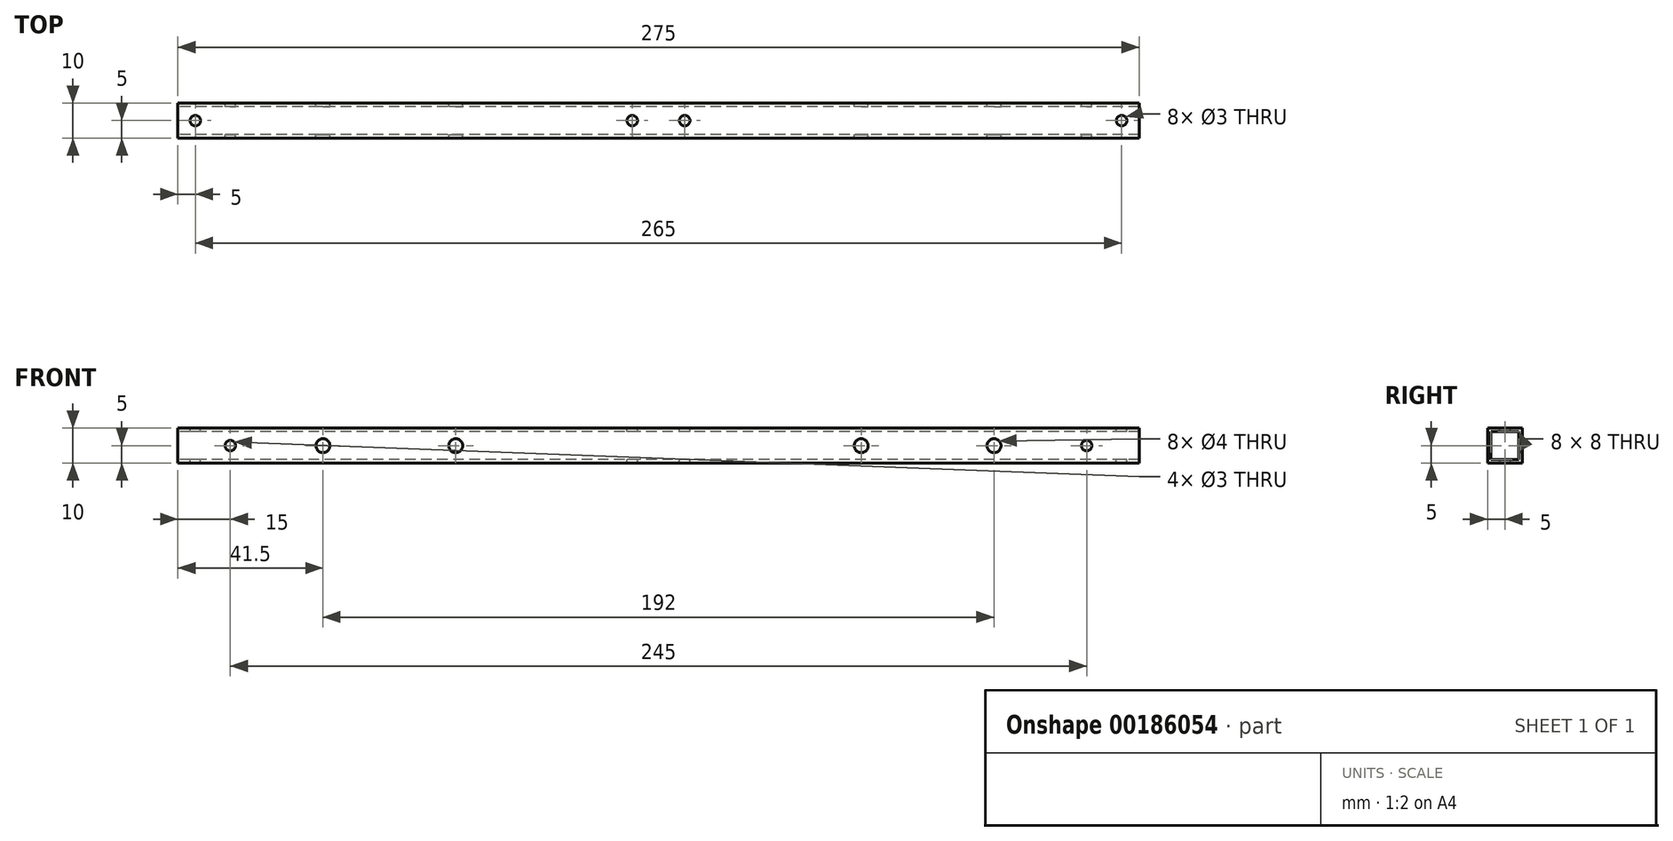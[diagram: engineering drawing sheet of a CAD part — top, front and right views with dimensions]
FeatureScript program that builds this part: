
annotation { "Feature Type Name" : "Feature", "Feature Type Description" : "" }
export const myFeature = defineFeature(function(context is Context, id is Id, definition is map)
    precondition{}
    {
        {
            var Q0;
            Q0=qCreatedBy(makeId("Right.planeOp"),FACE);
            var sketch = newSketch(context, id + "F0", { "sketchPlane" : qUnion([Q0])});
            skLineSegment(sketch, "E0.bottom", {"start": v(-5, -5) * mm, "end": v(5, -5) * mm});
            skLineSegment(sketch, "E0.top", {"start": v(-5, 5) * mm, "end": v(5, 5) * mm});
            skLineSegment(sketch, "E0.left", {"start": v(-5, -5) * mm, "end": v(-5, 5) * mm});
            skLineSegment(sketch, "E0.right", {"start": v(5, -5) * mm, "end": v(5, 5) * mm});
            skPoint(sketch, "E0.middle", {"position": v(0, 0) * mm});
            skLineSegment(sketch, "E1.bottom", {"start": v(-4, -4) * mm, "end": v(4, -4) * mm});
            skLineSegment(sketch, "E1.top", {"start": v(-4, 4) * mm, "end": v(4, 4) * mm});
            skLineSegment(sketch, "E1.left", {"start": v(-4, -4) * mm, "end": v(-4, 4) * mm});
            skLineSegment(sketch, "E1.right", {"start": v(4, -4) * mm, "end": v(4, 4) * mm});
            skSolve(sketch);
        }
        {
            var Q0;
            Q0 = qSketchRegion(id + "F0", true);
            extrude(context, id + "F1", {"entities" : qUnion([Q0]), "depth" : 275 * mm});
        }
        {
            var Q0;
            Q0=makeQuery(id+"F1.opExtrude","SWEPT_FACE",FACE,{"disambiguationData":[OSD([sQuery(id+"F0.wireOp",EDGE,"E0.top")])]});
            var sketch = newSketch(context, id + "F2", { "sketchPlane" : qUnion([Q0])});
            skLineSegment(sketch, "E2", {"start": v(0, 0) * mm, "end": v(275, 0) * mm, "construction": true});
            skLineSegment(sketch, "E3", {"start": v(137.5, -5) * mm, "end": v(137.5, 5) * mm, "construction": true});
            skCircle(sketch, "E4", {"center": v(130, 0) * mm, "radius": 1.5 * mm});
            skCircle(sketch, "E5", {"center": v(5, 0) * mm, "radius": 1.5 * mm});
            skCircle(sketch, "E6.MirrorC", {"center": v(145, 0) * mm, "radius": 1.5 * mm});
            skCircle(sketch, "E7.MirrorC", {"center": v(270, 0) * mm, "radius": 1.5 * mm});
            skSolve(sketch);
        }
        {
            var Q0;
            Q0 = qSketchRegion(id + "F2", true);
            extrude(context, id + "F3", {"entities" : qUnion([Q0]), "operationType" : NewBodyOperationType.REMOVE, "oppositeDirection" : true, "depth" : 25 * mm});
        }
        {
            var Q0;
            Q0=makeQuery(id+"F1.opExtrude","SWEPT_FACE",FACE,{"disambiguationData":[OSD([sQuery(id+"F0.wireOp",EDGE,"E0.right")])]});
            var sketch = newSketch(context, id + "F4", { "sketchPlane" : qUnion([Q0])});
            skLineSegment(sketch, "E8", {"start": v(-275, 0) * mm, "end": v(0, 0) * mm, "construction": true});
            skLineSegment(sketch, "E9", {"start": v(-137.5, 5) * mm, "end": v(-137.5, -5) * mm, "construction": true});
            skCircle(sketch, "E10", {"center": v(-233.5, 0) * mm, "radius": 2 * mm});
            skCircle(sketch, "E11", {"center": v(-195.5, 0) * mm, "radius": 2 * mm});
            skCircle(sketch, "E12.MirrorC", {"center": v(-79.5, 0) * mm, "radius": 2 * mm});
            skCircle(sketch, "E13.MirrorC", {"center": v(-41.5, 0) * mm, "radius": 2 * mm});
            skCircle(sketch, "E14", {"center": v(-260, 0) * mm, "radius": 1.5 * mm});
            skCircle(sketch, "E15.MirrorC", {"center": v(-15, 0) * mm, "radius": 1.5 * mm});
            skSolve(sketch);
        }
        {
            var Q0;
            Q0 = qSketchRegion(id + "F4", true);
            extrude(context, id + "F5", {"entities" : qUnion([Q0]), "operationType" : NewBodyOperationType.REMOVE, "oppositeDirection" : true, "depth" : 25 * mm});
        }
    });
